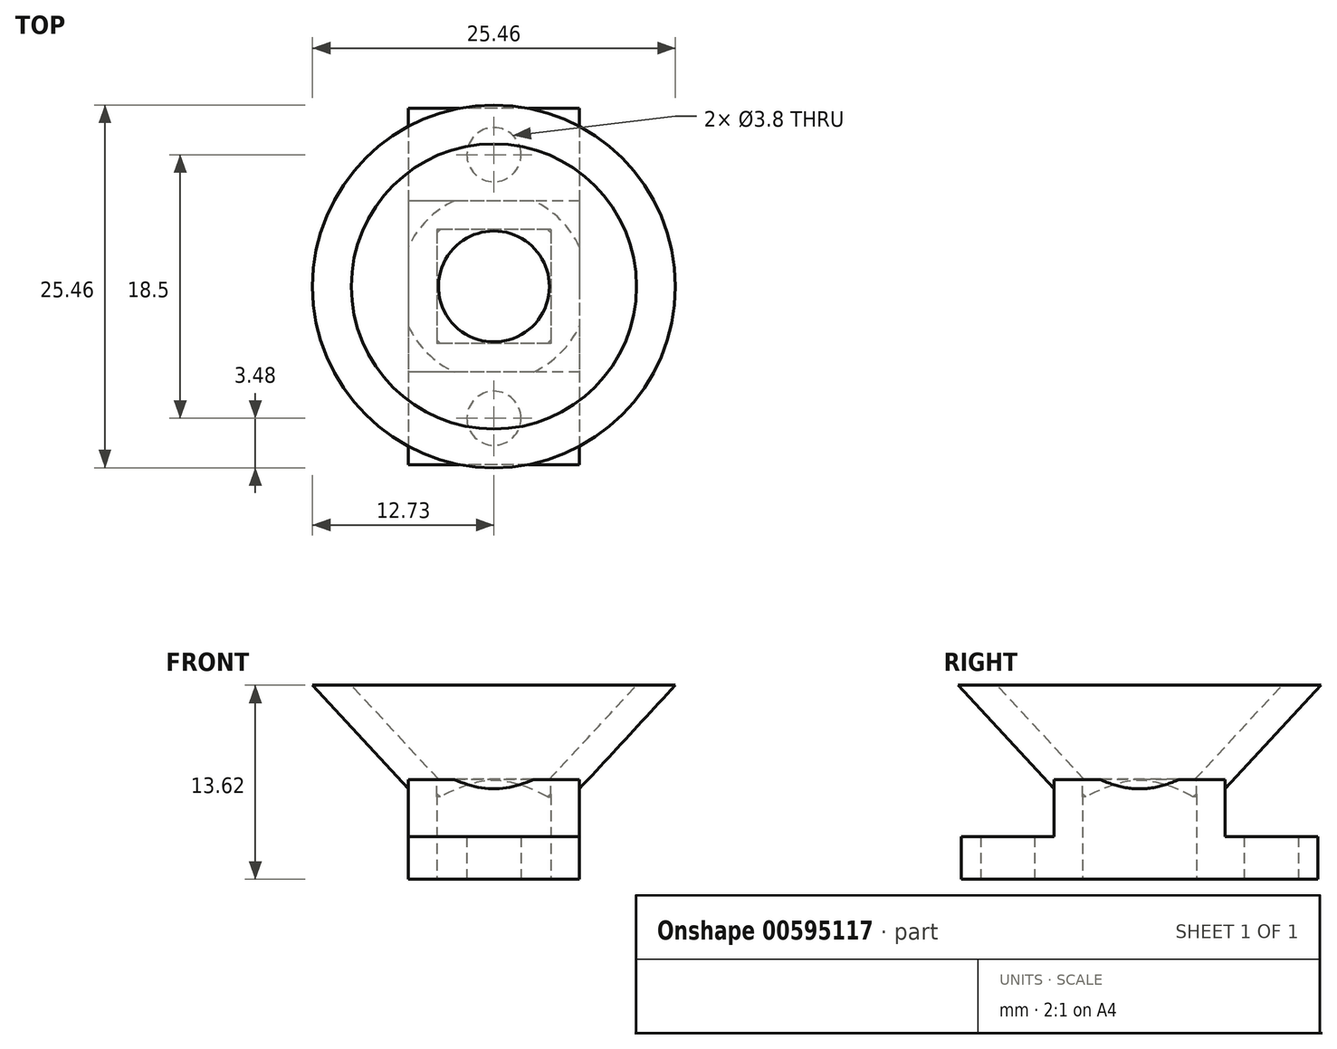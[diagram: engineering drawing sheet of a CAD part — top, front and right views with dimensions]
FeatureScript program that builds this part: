
annotation { "Feature Type Name" : "Feature", "Feature Type Description" : "" }
export const myFeature = defineFeature(function(context is Context, id is Id, definition is map)
    precondition{}
    {
        {
            var Q0;
            Q0=qCreatedBy(makeId("Top.planeOp"),FACE);
            var sketch = newSketch(context, id + "F0", { "sketchPlane" : qUnion([Q0])});
            skLineSegment(sketch, "E0.bottom", {"start": v(6, 12.5) * mm, "end": v(-6, 12.5) * mm});
            skLineSegment(sketch, "E0.top", {"start": v(6, -12.5) * mm, "end": v(-6, -12.5) * mm});
            skLineSegment(sketch, "E0.left", {"start": v(6, 12.5) * mm, "end": v(6, -12.5) * mm});
            skLineSegment(sketch, "E0.right", {"start": v(-6, 12.5) * mm, "end": v(-6, -12.5) * mm});
            skPoint(sketch, "E0.middle", {"position": v(0, 0) * mm});
            skCircle(sketch, "E1", {"center": v(0, 9.25) * mm, "radius": 1.9 * mm});
            skCircle(sketch, "E2", {"center": v(0, -9.25) * mm, "radius": 1.9 * mm});
            skLineSegment(sketch, "E3.bottom", {"start": v(4, 4) * mm, "end": v(-4, 4) * mm});
            skLineSegment(sketch, "E3.top", {"start": v(4, -4) * mm, "end": v(-4, -4) * mm});
            skLineSegment(sketch, "E3.left", {"start": v(4, 4) * mm, "end": v(4, -4) * mm});
            skLineSegment(sketch, "E3.right", {"start": v(-4, 4) * mm, "end": v(-4, -4) * mm});
            skSolve(sketch);
        }
        {
            var Q0;
            Q0=makeQuery(id+"F0.imprint","IMPRINT",FACE,{"disambiguationData":[TD([[makeQuery(id+"F0.imprint","IMPRINT",EDGE,{"derivedFrom":sQuery(id+"F0.wireOp",EDGE,"E0.bottom")}),1.0]])]});
            extrude(context, id + "F1", {"entities" : qUnion([Q0]), "depth" : 3 * mm, "offsetDistance" : 25 * mm});
        }
        {
            var Q0;
            Q0=makeQuery(id+"F1.opExtrude","CAP_FACE",FACE,{"disambiguationData":[OSD([sQuery(id+"F0.wireOp",EDGE,"E0.bottom"),sQuery(id+"F0.wireOp",EDGE,"E0.top"),sQuery(id+"F0.wireOp",EDGE,"E0.left"),sQuery(id+"F0.wireOp",EDGE,"E0.right"),sQuery(id+"F0.wireOp",EDGE,"E1"),sQuery(id+"F0.wireOp",EDGE,"E2"),sQuery(id+"F0.wireOp",EDGE,"E3.bottom"),sQuery(id+"F0.wireOp",EDGE,"E3.top"),sQuery(id+"F0.wireOp",EDGE,"E3.left"),sQuery(id+"F0.wireOp",EDGE,"E3.right")])],"isStart":false});
            var sketch = newSketch(context, id + "F2", { "sketchPlane" : qUnion([Q0])});
            skLineSegment(sketch, "E4.bottom", {"start": v(6, 6) * mm, "end": v(-6, 6) * mm});
            skLineSegment(sketch, "E4.top", {"start": v(6, -6) * mm, "end": v(-6, -6) * mm});
            skLineSegment(sketch, "E4.left", {"start": v(6, 6) * mm, "end": v(6, -6) * mm});
            skLineSegment(sketch, "E4.right", {"start": v(-6, 6) * mm, "end": v(-6, -6) * mm});
            skPoint(sketch, "E4.middle", {"position": v(0, 0) * mm});
            skSolve(sketch);
        }
        {
            var Q0;
            Q0=makeQuery(id+"F2.imprint","IMPRINT",FACE,{"disambiguationData":[TD([[makeQuery(id+"F2.imprint","IMPRINT",EDGE,{"derivedFrom":sQuery(id+"F2.wireOp",EDGE,"E4.bottom")}),1.0]])]});
            extrude(context, id + "F3", {"entities" : qUnion([Q0]), "operationType" : NewBodyOperationType.ADD, "depth" : 4 * mm, "offsetDistance" : 25 * mm});
        }
        {
            var Q0;
            Q0=makeQuery(id+"F3.opExtrude","CAP_FACE",FACE,{"disambiguationData":[OSD([sQuery(id+"F0.wireOp",EDGE,"E3.bottom"),sQuery(id+"F0.wireOp",EDGE,"E3.top"),sQuery(id+"F0.wireOp",EDGE,"E3.left"),sQuery(id+"F0.wireOp",EDGE,"E3.right"),sQuery(id+"F2.wireOp",EDGE,"E4.bottom"),sQuery(id+"F2.wireOp",EDGE,"E4.top"),sQuery(id+"F2.wireOp",EDGE,"E4.left"),sQuery(id+"F2.wireOp",EDGE,"E4.right")])],"isStart":false});
            var sketch = newSketch(context, id + "F4", { "sketchPlane" : qUnion([Q0])});
            skCircle(sketch, "E5", {"center": v(0, 0) * mm, "radius": 4.5 * mm});
            skCircle(sketch, "E6", {"center": v(0, 0) * mm, "radius": 6 * mm});
            skSolve(sketch);
        }
        {
            var Q0;
            Q0=qCreatedBy(makeId("Right.planeOp"),FACE);
            var sketch = newSketch(context, id + "F5", { "sketchPlane" : qUnion([Q0])});
            skLineSegment(sketch, "E7", {"start": v(3.68, 3.83) * mm, "end": v(14.17, 15.18) * mm});
            skLineSegment(sketch, "E8", {"start": v(1.06, 3.94) * mm, "end": v(11.66, 15.41) * mm});
            skLineSegment(sketch, "E9", {"start": v(8.85, 13.62) * mm, "end": v(13.51, 13.62) * mm});
            skLineSegment(sketch, "E10", {"start": v(3.9, 7) * mm, "end": v(5.5, 5.8) * mm});
            skLineSegment(sketch, "E11", {"start": v(0, 20.37) * mm, "end": v(0, -5.63) * mm, "construction": true});
            skSolve(sketch);
        }
        {
            var Q0;
            {var subQ0=sQuery(id+"F5.wireOp",EDGE,"E10");Q0=makeQuery(id+"F5.imprint","IMPRINT",FACE,{"disambiguationData":[TD([[makeQuery(id+"F5.imprint","IMPRINT",EDGE,{"derivedFrom":subQ0}),1.0]])]});}
            var Q1;
            Q1=sQuery(id+"F5.wireOp",EDGE,"E11");
            revolve(context, id + "F6", {"operationType" : NewBodyOperationType.ADD, "entities" : qUnion([Q0]), "axis" : qUnion([Q1]), "revolveType" : RevolveType.FULL});
        }
    });
